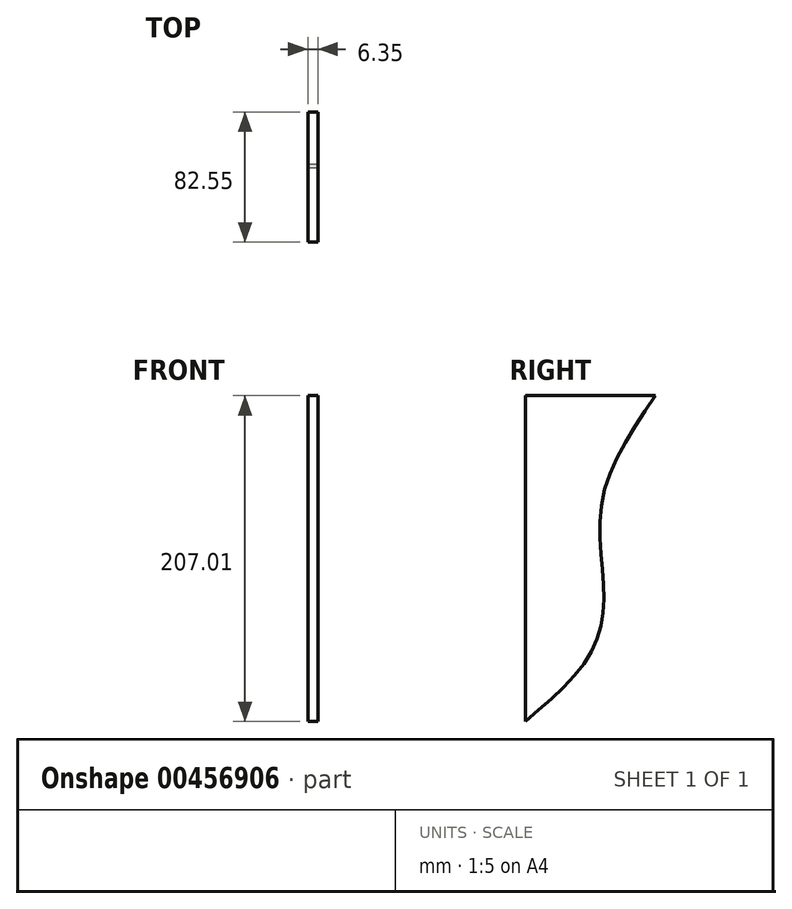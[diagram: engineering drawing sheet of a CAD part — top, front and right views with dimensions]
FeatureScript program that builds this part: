
annotation { "Feature Type Name" : "Feature", "Feature Type Description" : "" }
export const myFeature = defineFeature(function(context is Context, id is Id, definition is map)
    precondition{}
    {
        {
            var Q0;
            Q0=qCreatedBy(makeId("Right.planeOp"),FACE);
            var sketch = newSketch(context, id + "F0", { "sketchPlane" : qUnion([Q0])});
            skLineSegment(sketch, "E0.bottom", {"start": v(-94.16, 97.02) * mm, "end": v(-11.6, 97.02) * mm});
            skLineSegment(sketch, "E0.top", {"start": v(-94.16, -110) * mm, "end": v(-11.6, -110) * mm});
            skLineSegment(sketch, "E0.left", {"start": v(-94.16, 97.02) * mm, "end": v(-94.16, -110) * mm});
            skLineSegment(sketch, "E1", {"start": v(-11.6, -110) * mm, "end": v(-11.6, 97.02) * mm});
            skSolve(sketch);
        }
        {
            var Q0;
            Q0=makeQuery(id+"F0.imprint","IMPRINT",FACE,{"disambiguationData":[TD([[makeQuery(id+"F0.imprint","IMPRINT",EDGE,{"derivedFrom":sQuery(id+"F0.wireOp",EDGE,"E0.bottom")}),-1.0]])]});
            extrude(context, id + "F1", {"entities" : qUnion([Q0]), "depth" : 6.35 * mm});
        }
        {
            var Q0;
            Q0=makeQuery(id+"F1.opExtrude","CAP_FACE",FACE,{"disambiguationData":[OSD([sQuery(id+"F0.wireOp",EDGE,"E0.bottom"),sQuery(id+"F0.wireOp",EDGE,"E0.top"),sQuery(id+"F0.wireOp",EDGE,"E0.left"),sQuery(id+"F0.wireOp",EDGE,"E1")])],"isStart":false});
            var sketch = newSketch(context, id + "F2", { "sketchPlane" : qUnion([Q0])});
            skPoint(sketch, "E2", {"position": v(-68.76, -110) * mm});
            skPoint(sketch, "E3", {"position": v(-52.88, -110) * mm});
            skPoint(sketch, "E4", {"position": v(-30.66, -110) * mm});
            skPoint(sketch, "E5", {"position": v(-68.76, 97.02) * mm});
            skPoint(sketch, "E6", {"position": v(-52.88, 97.02) * mm});
            skPoint(sketch, "E7", {"position": v(-30.66, 97.02) * mm});
            skPoint(sketch, "E8", {"position": v(-11.6, -66.65) * mm});
            skPoint(sketch, "E9", {"position": v(-11.6, -24.6) * mm});
            skPoint(sketch, "E10", {"position": v(-11.6, 32.65) * mm});
            skFitSpline(sketch, "E11", {"points": [v(-94.16, -110) * mm, v(-52.88, -66.65) * mm, v(-44.63, -24.6) * mm, v(-45.1, 32.65) * mm, v(-11.6, 97.02) * mm], "startDerivative": vector(192.65, 165.44) * mm, "endDerivative": vector(154.79, 227.05) * mm});
            skSolve(sketch);
        }
        {
            var Q0;
            Q0=makeQuery(id+"F2.imprint","IMPRINT",FACE,{"disambiguationData":[TD([[makeQuery(id+"F2.imprint","IMPRINT",EDGE,{"derivedFrom":sQuery(id+"F2.wireOp",EDGE,"E11")}),-1.0]])]});
            extrude(context, id + "F3", {"entities" : qUnion([Q0]), "operationType" : NewBodyOperationType.REMOVE, "oppositeDirection" : true, "depth" : 12.7 * mm});
        }
    });
